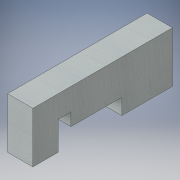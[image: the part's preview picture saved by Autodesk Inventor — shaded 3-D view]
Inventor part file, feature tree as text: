
AUTODESK INVENTOR PART (.ipt)
format: ipt  version: 2016 (Build 200138000, 138)  size: 120,832 bytes
history: native  units: in
note: dims shown in document units (in); Inventor stores cm internally (conversion verified against a paired STEP export)
features: extrude x2, sketch x2
ambient origin geometry x8: Origin, YZ Plane, XZ Plane, XY Plane, X Axis, Y Axis, Z Axis, Center Point
bodies: Solid1 (feature_tree)
feature tree (4):
  extrude  "Extrusion1"  Depth=4.0in
  extrude  "Extrusion2"  Depth=1.0in
  sketch  "Sketch1"  dims[d0=2.0in d1=4.0in]
  sketch  "Sketch2"  dims[d2=11.0in d3=0.0in d4=1.0in d5=2.25in d6=2.0in d7=4.0in d8=1.25in d9=11.0in d10=0.0in]
